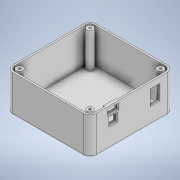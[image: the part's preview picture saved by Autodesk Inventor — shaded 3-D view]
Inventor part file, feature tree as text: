
AUTODESK INVENTOR PART (.ipt)
format: ipt  version: 2020 (Build 240168000, 168)  size: 249,344 bytes
history: native  units: in
note: dims shown in document units (in); Inventor stores cm internally (conversion verified against a paired STEP export)
features: extrude x6, sketch x6, projected_geometry x5, mirror x2, chamfer x2, shell x1, fillet x1
ambient origin geometry x8: Origin, YZ Plane, XZ Plane, XY Plane, X Axis, Y Axis, Z Axis, Center Point
bodies: Solid1 (feature_tree)
feature tree (23):
  extrude  "Extrusion1"  Depth=3.1496in
  shell  "Shell1"  Thickness=0.25in
  fillet  "Fillet1"  Radius=1.0in
  extrude  "Extrusion2"  Depth=0.05in
  mirror  "Mirror1"
  mirror  "Mirror2"
  extrude  "Extrusion4"  Depth=0.25in
  extrude  "Extrusion5"  Depth=0.3937in TaperAngle=0.0deg
  extrude  "Extrusion6"  Depth=0.5in
  chamfer  "Chamfer1"  Distance=0.3937in
  extrude  "Extrusion7"  Depth=0.1575in
  chamfer  "Chamfer2"  Distance=0.0689in
  sketch  "Sketch1"  dims[d0=3.1496in d1=3.1496in d2=0.25in d3=1.0in d4=0.0in]
  sketch  "Sketch2"  dims[d5=0.0669in d6=0.05in]
  sketch  "Sketch4"  dims[d7=0.25in d8=0.0945in]
  projected_geometry  "Projected Loop1"
  projected_geometry  "Projected Loop2"
  projected_geometry  "Projected Loop3"
  projected_geometry  "Projected Loop4"
  projected_geometry  "Projected Loop5"
  sketch  "Sketch5"  dims[d9=1.0in d10=0.0in d16=0.3937in d17=0.0in]
  sketch  "Sketch6"  dims[d18=0.05in d19=0.5in d20=0.3937in d21=0.0in]
  sketch  "Sketch7"  dims[d22=0.3543in d23=0.1575in d24=0.0689in d25=0.1181in d26=0.252in d27=0.252in d28=0.1181in d29=0.3937in d30=0.0in d31=0.0394in d32=0.125in d33=45.0deg d34=0.31in d35=0.51in d36=0.25in d37=0.3in d38=1.0in d39=0.0in d40=0.03in d41=0.125in d42=45.0deg]
